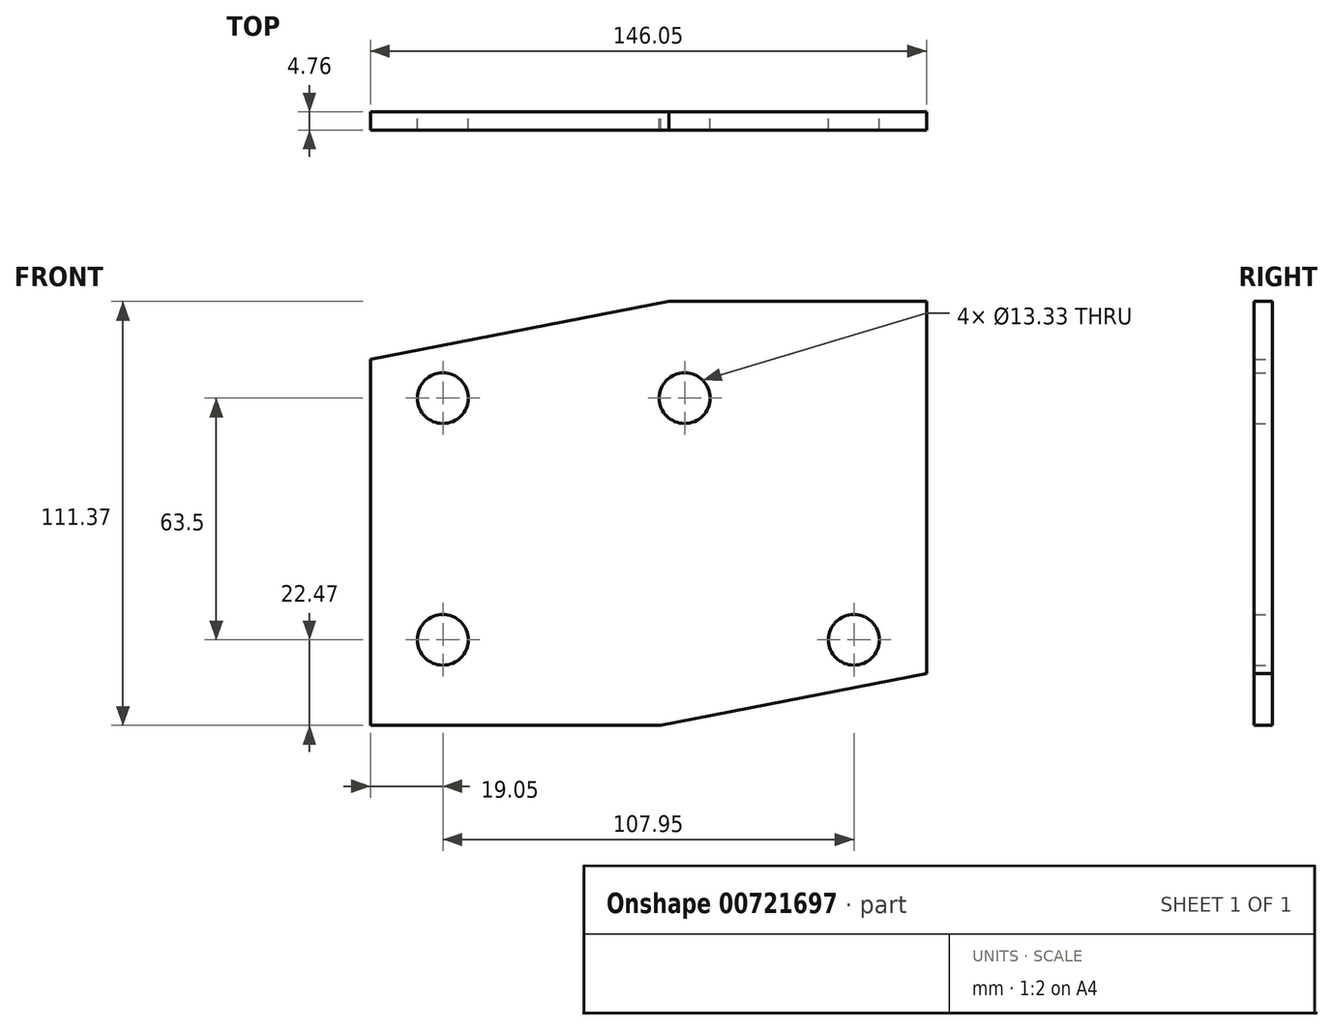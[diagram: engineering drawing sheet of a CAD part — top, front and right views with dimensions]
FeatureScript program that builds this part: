
annotation { "Feature Type Name" : "Feature", "Feature Type Description" : "" }
export const myFeature = defineFeature(function(context is Context, id is Id, definition is map)
    precondition{}
    {
        {
            var Q0;
            Q0=qCreatedBy(makeId("Front.planeOp"),FACE);
            var sketch = newSketch(context, id + "F0", { "sketchPlane" : qUnion([Q0])});
            skLineSegment(sketch, "E0.right", {"start": v(-146.05, 82.55) * mm, "end": v(-146.05, -13.58) * mm});
            skPoint(sketch, "E0.middle", {"position": v(0, -37.4) * mm});
            skCircle(sketch, "E1", {"center": v(-63.5, 72.4) * mm, "radius": 6.67 * mm});
            skCircle(sketch, "E2", {"center": v(-19.05, 8.9) * mm, "radius": 6.67 * mm});
            skPoint(sketch, "E3.startSnap0", {"position": v(-146.05, 34.49) * mm});
            skLineSegment(sketch, "E4", {"start": v(-156.26, 40.64) * mm, "end": v(11.3, 40.64) * mm, "construction": true});
            skLineSegment(sketch, "E5", {"start": v(0, 97.8) * mm, "end": v(0, 0) * mm});
            skLineSegment(sketch, "E6", {"start": v(0, 0) * mm, "end": v(-69.85, -13.58) * mm});
            skLineSegment(sketch, "E7", {"start": v(-19.05, -31.54) * mm, "end": v(-19.05, 107.9) * mm, "construction": true});
            skLineSegment(sketch, "E8", {"start": v(-69.85, -13.58) * mm, "end": v(-146.05, -13.58) * mm});
            skLineSegment(sketch, "E9", {"start": v(27.7, 8.9) * mm, "end": v(-152.82, 8.9) * mm, "construction": true});
            skLineSegment(sketch, "E10", {"start": v(-154.82, 72.39) * mm, "end": v(12.9, 72.4) * mm, "construction": true});
            skLineSegment(sketch, "E11", {"start": v(-127, 115.5) * mm, "end": v(-127, -28.35) * mm, "construction": true});
            skCircle(sketch, "E12", {"center": v(-127, 72.39) * mm, "radius": 6.67 * mm});
            skCircle(sketch, "E13", {"center": v(-127, 8.9) * mm, "radius": 6.67 * mm});
            skLineSegment(sketch, "E14", {"start": v(-146.05, 82.55) * mm, "end": v(-67.65, 97.8) * mm});
            skLineSegment(sketch, "E15", {"start": v(-67.65, 97.8) * mm, "end": v(0, 97.8) * mm});
            skSolve(sketch);
        }
        {
            var Q0;
            Q0=qSketchRegion(id+"F0",true);
            extrude(context, id + "F1", {"entities" : qUnion([Q0]), "depth" : 4.76 * mm, "offsetDistance" : 25.4 * mm});
        }
    });
